# Revit family: Zumtobel LINETIK-S
name_source: partatom
category: Lighting Fixtures
revit_build: Autodesk Revit 2016 (Build: 20150220_1215(x64)
units: mm (PartAtom-declared; Revit-internal decimal feet)

## family parameters
Always vertical = Yes
Cut with Voids When Loaded = No
Light Source = Yes
OmniClass Number = 23.80.70.11
OmniClass Title = Luminaries for Internal Lighting
Part Type = Normal
Room Calculation Point = No
Round Connector Dimension = Use Diameter
Shared = No
Work Plane-Based = No

## types (2) — shared parameters
Apparent Load = 2 VA
Assembly Code = D5020210
Color Filter = 16777215
Cover = Zumtobel_Cover_Self_llumination_Opaque
Description = Free-standing LED luminaire
Dimming Lamp Color Temperature Shift = <None>
Emit Shape Visible in Rendering = No
Emit from Rectangle Length = 13 mm
Emit from Rectangle Width = 1000 mm  [stored 3.28084 ft]
Height = 2225 mm
Lamp = LED
Length = 630 mm  [stored 2.06693 ft]
Manufacturer = Zumtobel Lighting
Photometric Web File = 42185542_(IND_LEO1_I_D).IES
Tilt Angle = -90.00°
URL = http://www.zumtobel.com
Voltage = 230 V
Width = 300 mm

## per-type parameters (varying)
| type | Body | Model |
| LINETIK-S D/I LED BK | Zumtobel_Metal_Black | 42185542 |
| LINETIK-S D/I LED WH | Zumtobel_Metal_White | 42184503 |

note: [stored X ft] marks values corroborated as IEEE doubles in the binary element streams (Revit-internal decimal feet)

## geometry (parser evidence)
native form markers: Sweep x2
no freeform markers — native parametric forms only
